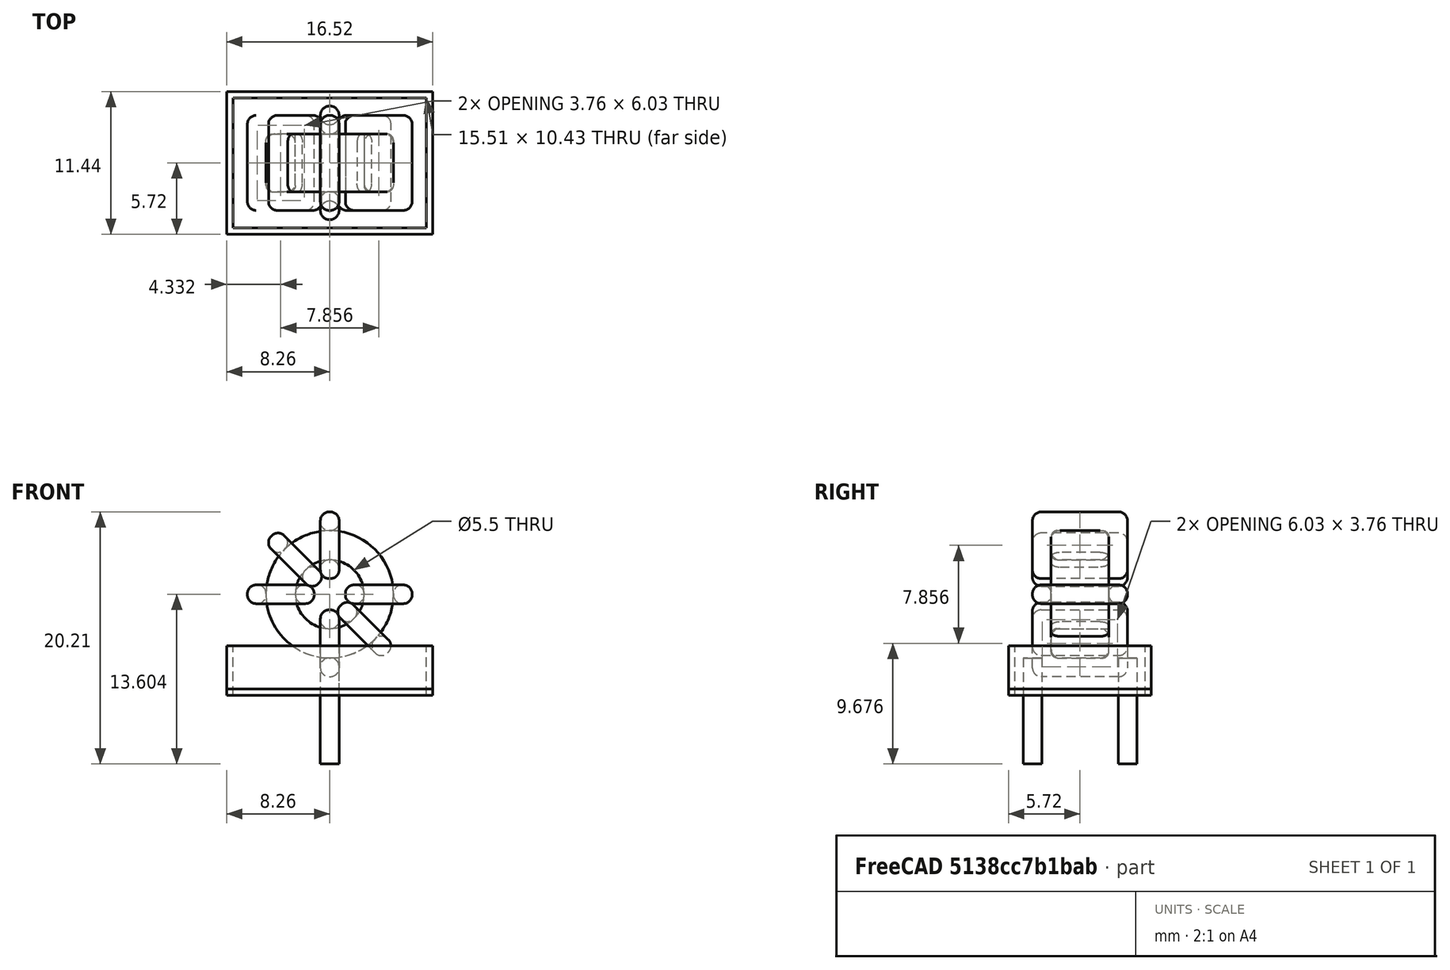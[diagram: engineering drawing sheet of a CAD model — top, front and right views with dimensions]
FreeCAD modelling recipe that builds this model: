
FCSTD DOCUMENT  (FreeCAD 0.16R6703 (Git))
Label: L_Toroid_Vertical_L16.5mm_W11.4mm_P7.62mm_Pulse_KM-2
License: All rights reserved
LicenseURL: http://en.wikipedia.org/wiki/All_rights_reserved
objects: Sketcher::SketchObject×8, PartDesign::Pad×8, PartDesign::Fillet×5, Spreadsheet::Sheet×1
note: 29 computed .brp shape members not serialized (recipe doc carries the construction recipe); baked Part::Feature solids carry a one-line shape summary decoded from their .brp

FEATURE [Spreadsheet::Sheet] Spreadsheet  label="dimensions"
  cells = A1=Wx; B1(Wx)=13.208; C1(WW)=5.503333333333334; D1(iWx)=16.51; A2=Wy; B2(Wy)=7.62; D2(iWy)=11.43; A3=RM; B3(RMx)=7.62; C3(RMy)=0; A4=d_wire; B4(d_wire)=1.5; A5=H; B5(H)=16.51; A6=offsetx; B6(offsetx)=8.255000000000001
FEATURE [Sketcher::SketchObject] Sketch
  Placement = pos=(0,-3.81,0) rot=(1,0,0;1.5708rad)
  expr: Placement.Base.y = -Spreadsheet.RMx / 2
  expr: Constraints[0] = Spreadsheet.Wx / 2 - Spreadsheet.d_wire
  expr: Constraints[4] = Spreadsheet.WW / 2
  expr: Constraints[2] = Spreadsheet.Wx / 2 + Spreadsheet.d_wire + 0.5
  sketch-geometry (2):
    g0: Circle CenterX=0 CenterY=8.604 CenterZ=0 NormalX=0 NormalY=0 NormalZ=1 Radius=5.104
    g1: Circle CenterX=0 CenterY=8.604 CenterZ=0 NormalX=0 NormalY=0 NormalZ=1 Radius=2.75167
  constraints (5):
    c: Radius(g0) = 5.104
    c: DistanceX(g-1,g0) = 0
    c: DistanceY(g-1,g0) = 8.604
    c: Coincident(g1,g0)
    c: Radius(g1) = 2.75167
FEATURE [PartDesign::Pad] Pad
  Length = 4.62
  Length2 = 100
  Midplane = true
  Placement = pos=(0,-3.81,0) rot=(1,0,0;1.5708rad)
  Sketch = -> Sketch
  Type = 0
  expr: Length = Spreadsheet.Wy - 2 * Spreadsheet.d_wire
FEATURE [Sketcher::SketchObject] Sketch001
  Placement = pos=(0,0,2) rot=(0,0,1;0rad)
  expr: Placement.Base.z = 0.5 + Spreadsheet.d_wire
  expr: Constraints[4] = Spreadsheet.RMy
  expr: Constraints[2] = -Spreadsheet.RMx
  expr: Constraints[1] = Spreadsheet.d_wire / 2
  sketch-geometry (2):
    g0: Circle CenterX=0 CenterY=0 CenterZ=0 NormalX=0 NormalY=0 NormalZ=1 Radius=0.75
    g1: Circle CenterX=0 CenterY=-7.62 CenterZ=0 NormalX=0 NormalY=0 NormalZ=1 Radius=0.75
  constraints (5):
    c: Equal(g0,g1)
    c: Radius(g0) = 0.75
    c: DistanceY(g-1,g1) = -7.62
    c: Coincident(g0,g-1)
    c: DistanceX(g-1,g1) = 0
FEATURE [PartDesign::Pad] Pad001
  Length = 1.5
  Length2 = 7
  Placement = pos=(0,0,2) rot=(0,0,1;0rad)
  Reversed = true
  Sketch = -> Sketch001
  Type = 4
  expr: Length2 = 5.5 + Spreadsheet.d_wire
  expr: Length = Spreadsheet.d_wire
FEATURE [PartDesign::Fillet] Fillet
  Base = -> Pad [Edge6,Edge3,Edge2]
  Placement = pos=(0,-3.81,0) rot=(1,0,0;1.5708rad)
  Radius = 0.5
FEATURE [Sketcher::SketchObject] Sketch003
  Placement = pos=(0,0,8.604) rot=(1,0,0;3.14159rad)
  expr: Constraints[18] = Spreadsheet.d_wire
  expr: Constraints[16] = Spreadsheet.d_wire
  expr: Constraints[19] = Spreadsheet.d_wire
  expr: Constraints[17] = Spreadsheet.d_wire
  expr: Placement.Base.y = -1 * (Spreadsheet.RMx - Spreadsheet.Wy) / 2
  expr: Constraints[21] = (Spreadsheet.Wx - Spreadsheet.WW) / 2 - Spreadsheet.d_wire
  expr: Constraints[22] = Spreadsheet.Wx / 2 - Spreadsheet.d_wire
  expr: Constraints[43] = Spreadsheet.d_wire
  expr: Constraints[48] = Spreadsheet.Wx - Spreadsheet.d_wire * 2
  expr: Constraints[49] = Spreadsheet.Wy
  expr: Placement.Base.z = Spreadsheet.Wx / 2 + Spreadsheet.d_wire + 0.5
  sketch-geometry (16):
    g0: LineSegment StartX=-1.25167 StartY=0 StartZ=0 EndX=-6.604 EndY=0 EndZ=0
    g1: LineSegment StartX=-6.604 StartY=0 StartZ=0 EndX=-6.604 EndY=7.62 EndZ=0
    g2: LineSegment StartX=-6.604 StartY=7.62 StartZ=0 EndX=-1.25167 EndY=7.62 EndZ=0
    g3: LineSegment StartX=-1.25167 StartY=7.62 StartZ=0 EndX=-1.25167 EndY=0 EndZ=0
    g4: LineSegment StartX=-5.104 StartY=6.12 StartZ=0 EndX=-2.75167 EndY=6.12 EndZ=0
    g5: LineSegment StartX=-2.75167 StartY=6.12 StartZ=0 EndX=-2.75167 EndY=1.5 EndZ=0
    g6: LineSegment StartX=-2.75167 StartY=1.5 StartZ=0 EndX=-5.104 EndY=1.5 EndZ=0
    g7: LineSegment StartX=-5.104 StartY=1.5 StartZ=0 EndX=-5.104 EndY=6.12 EndZ=0
    g8: LineSegment StartX=1.25167 StartY=7.62 StartZ=0 EndX=6.604 EndY=7.62 EndZ=0
    g9: LineSegment StartX=6.604 StartY=7.62 StartZ=0 EndX=6.604 EndY=0 EndZ=0
    g10: LineSegment StartX=6.604 StartY=0 StartZ=0 EndX=1.25167 EndY=0 EndZ=0
    g11: LineSegment StartX=1.25167 StartY=0 StartZ=0 EndX=1.25167 EndY=7.62 EndZ=0
    g12: LineSegment StartX=2.75167 StartY=6.12 StartZ=0 EndX=5.104 EndY=6.12 EndZ=0
    g13: LineSegment StartX=5.104 StartY=6.12 StartZ=0 EndX=5.104 EndY=1.5 EndZ=0
    g14: LineSegment StartX=5.104 StartY=1.5 StartZ=0 EndX=2.75167 EndY=1.5 EndZ=0
    g15: LineSegment StartX=2.75167 StartY=1.5 StartZ=0 EndX=2.75167 EndY=6.12 EndZ=0
  constraints (50):
    c: Horizontal(g0)
    c: Coincident(g1,g0)
    c: Vertical(g1)
    c: Coincident(g2,g1)
    c: Horizontal(g2)
    c: Coincident(g3,g2)
    c: Coincident(g3,g0)
    c: Vertical(g3)
    c: Coincident(g4,g5)
    c: Coincident(g5,g6)
    c: Coincident(g6,g7)
    c: Coincident(g7,g4)
    c: Horizontal(g4)
    c: Horizontal(g6)
    c: Vertical(g5)
    c: Vertical(g7)
    c: DistanceX(g1,g4) = 1.5
    c: DistanceY(g4,g1) = 1.5
    c: DistanceX(g5,g0) = 1.5
    c: DistanceY(g0,g5) = 1.5
    c: DistanceY(g-1,g0) = 0
    c: DistanceX(g6,g6) = 2.35233
    c: DistanceX(g6,g-1) = 5.104
    c: Coincident(g8,g9)
    c: Coincident(g9,g10)
    c: Coincident(g10,g11)
    c: Coincident(g11,g8)
    c: Horizontal(g8)
    c: Horizontal(g10)
    c: Vertical(g9)
    c: Vertical(g11)
    c: Coincident(g12,g13)
    c: Coincident(g13,g14)
    c: Coincident(g14,g15)
    c: Coincident(g15,g12)
    c: Horizontal(g12)
    c: Horizontal(g14)
    c: Vertical(g13)
    c: Vertical(g15)
    c: DistanceY(g8,g2) = 0
    c: DistanceY(g10,g0) = 0
    c: DistanceY(g14,g5) = 0
    c: DistanceY(g12,g4) = 0
    c: DistanceX(g8,g12) = 1.5
    c: Equal(g8,g2)
    c: Equal(g12,g4)
    c: Equal(g9,g1)
    c: Equal(g13,g7)
    c: DistanceX(g4,g12) = 10.208
    c: DistanceY(g0,g1) = 7.62
FEATURE [PartDesign::Pad] Pad002
  Length = 1.5
  Length2 = 100
  Midplane = true
  Placement = pos=(0,0,8.604) rot=(1,0,0;3.14159rad)
  Sketch = -> Sketch003
  Type = 0
  expr: Length = Spreadsheet.d_wire
FEATURE [PartDesign::Fillet] Fillet001
  Base = -> Pad002 [Edge38,Edge41,Edge42,Edge43,Edge29,Edge32,Edge33,Edge34,Edge25,Edge35,Edge36,Edge13,Edge14,Edge15,Edge16,Edge17,Edge18,Edge19,Edge1,Edge2,Edge3,Edge4,Edge5,Edge6,Edge7,Edge37,Edge39,Edge40,Edge20,Edge23,Edge24,Edge21,Edge22,Edge8,Edge9,Edge10,Edge11,Edge12,Edge26,Edge27,+8 more]
  Placement = pos=(0,0,8.604) rot=(1,0,0;3.14159rad)
  Radius = 0.705
  expr: Radius = Spreadsheet.d_wire * 0.47
FEATURE [Sketcher::SketchObject] Sketch004
  Placement = pos=(0,0,8.604) rot=(0.92388,0,0.382683;3.14159rad)
  expr: Constraints[18] = Spreadsheet.d_wire
  expr: Constraints[16] = Spreadsheet.d_wire
  expr: Constraints[19] = Spreadsheet.d_wire
  expr: Constraints[17] = Spreadsheet.d_wire
  expr: Placement.Base.y = -1 * (Spreadsheet.RMx - Spreadsheet.Wy) / 2
  expr: Constraints[21] = (Spreadsheet.Wx - Spreadsheet.WW) / 2 - Spreadsheet.d_wire
  expr: Constraints[22] = Spreadsheet.Wx / 2 - Spreadsheet.d_wire
  expr: Constraints[43] = Spreadsheet.d_wire
  expr: Constraints[48] = Spreadsheet.Wx - 2 * Spreadsheet.d_wire
  expr: Constraints[49] = Spreadsheet.Wy
  expr: Placement.Base.z = Spreadsheet.Wx / 2 + Spreadsheet.d_wire + 0.5
  sketch-geometry (16):
    g0: LineSegment StartX=-1.25167 StartY=0 StartZ=0 EndX=-6.604 EndY=0 EndZ=0
    g1: LineSegment StartX=-6.604 StartY=0 StartZ=0 EndX=-6.604 EndY=7.62 EndZ=0
    g2: LineSegment StartX=-6.604 StartY=7.62 StartZ=0 EndX=-1.25167 EndY=7.62 EndZ=0
    g3: LineSegment StartX=-1.25167 StartY=7.62 StartZ=0 EndX=-1.25167 EndY=0 EndZ=0
    g4: LineSegment StartX=-5.104 StartY=6.12 StartZ=0 EndX=-2.75167 EndY=6.12 EndZ=0
    g5: LineSegment StartX=-2.75167 StartY=6.12 StartZ=0 EndX=-2.75167 EndY=1.5 EndZ=0
    g6: LineSegment StartX=-2.75167 StartY=1.5 StartZ=0 EndX=-5.104 EndY=1.5 EndZ=0
    g7: LineSegment StartX=-5.104 StartY=1.5 StartZ=0 EndX=-5.104 EndY=6.12 EndZ=0
    g8: LineSegment StartX=1.25167 StartY=7.62 StartZ=0 EndX=6.604 EndY=7.62 EndZ=0
    g9: LineSegment StartX=6.604 StartY=7.62 StartZ=0 EndX=6.604 EndY=0 EndZ=0
    g10: LineSegment StartX=6.604 StartY=0 StartZ=0 EndX=1.25167 EndY=0 EndZ=0
    g11: LineSegment StartX=1.25167 StartY=0 StartZ=0 EndX=1.25167 EndY=7.62 EndZ=0
    g12: LineSegment StartX=2.75167 StartY=6.12 StartZ=0 EndX=5.104 EndY=6.12 EndZ=0
    g13: LineSegment StartX=5.104 StartY=6.12 StartZ=0 EndX=5.104 EndY=1.5 EndZ=0
    g14: LineSegment StartX=5.104 StartY=1.5 StartZ=0 EndX=2.75167 EndY=1.5 EndZ=0
    g15: LineSegment StartX=2.75167 StartY=1.5 StartZ=0 EndX=2.75167 EndY=6.12 EndZ=0
  constraints (50):
    c: Horizontal(g0)
    c: Coincident(g1,g0)
    c: Vertical(g1)
    c: Coincident(g2,g1)
    c: Horizontal(g2)
    c: Coincident(g3,g2)
    c: Coincident(g3,g0)
    c: Vertical(g3)
    c: Coincident(g4,g5)
    c: Coincident(g5,g6)
    c: Coincident(g6,g7)
    c: Coincident(g7,g4)
    c: Horizontal(g4)
    c: Horizontal(g6)
    c: Vertical(g5)
    c: Vertical(g7)
    c: DistanceX(g1,g4) = 1.5
    c: DistanceY(g4,g1) = 1.5
    c: DistanceX(g5,g0) = 1.5
    c: DistanceY(g0,g5) = 1.5
    c: DistanceY(g-1,g0) = 0
    c: DistanceX(g6,g6) = 2.35233
    c: DistanceX(g6,g-1) = 5.104
    c: Coincident(g8,g9)
    c: Coincident(g9,g10)
    c: Coincident(g10,g11)
    c: Coincident(g11,g8)
    c: Horizontal(g8)
    c: Horizontal(g10)
    c: Vertical(g9)
    c: Vertical(g11)
    c: Coincident(g12,g13)
    c: Coincident(g13,g14)
    c: Coincident(g14,g15)
    c: Coincident(g15,g12)
    c: Horizontal(g12)
    c: Horizontal(g14)
    c: Vertical(g13)
    c: Vertical(g15)
    c: DistanceY(g8,g2) = 0
    c: DistanceY(g10,g0) = 0
    c: DistanceY(g14,g5) = 0
    c: DistanceY(g12,g4) = 0
    c: DistanceX(g8,g12) = 1.5
    c: Equal(g8,g2)
    c: Equal(g12,g4)
    c: Equal(g9,g1)
    c: Equal(g13,g7)
    c: DistanceX(g4,g12) = 10.208
    c: DistanceY(g0,g1) = 7.62
FEATURE [PartDesign::Pad] Pad003
  Length = 1.5
  Length2 = 100
  Midplane = true
  Placement = pos=(0,0,8.604) rot=(0.92388,0,0.382683;3.14159rad)
  Sketch = -> Sketch004
  Type = 0
  expr: Length = Spreadsheet.d_wire
FEATURE [PartDesign::Fillet] Fillet002
  Base = -> Pad003 [Edge38,Edge41,Edge42,Edge43,Edge29,Edge32,Edge33,Edge34,Edge25,Edge35,Edge36,Edge13,Edge14,Edge15,Edge16,Edge17,Edge18,Edge19,Edge1,Edge2,Edge3,Edge4,Edge5,Edge6,Edge7,Edge37,Edge39,Edge40,Edge20,Edge23,Edge24,Edge21,Edge22,Edge8,Edge9,Edge10,Edge11,Edge12,Edge26,Edge27,+8 more]
  Placement = pos=(0,0,8.604) rot=(0.92388,0,0.382683;3.14159rad)
  Radius = 0.705
  expr: Radius = Spreadsheet.d_wire * 0.47
FEATURE [Sketcher::SketchObject] Sketch005
  Placement = pos=(0,0,8.604) rot=(0.92388,0,-0.382683;3.14159rad)
  expr: Constraints[18] = Spreadsheet.d_wire
  expr: Constraints[16] = Spreadsheet.d_wire
  expr: Constraints[19] = Spreadsheet.d_wire
  expr: Constraints[17] = Spreadsheet.d_wire
  expr: Placement.Base.y = -1 * (Spreadsheet.RMx - Spreadsheet.Wy) / 2
  expr: Constraints[21] = (Spreadsheet.Wx - Spreadsheet.WW) / 2 - Spreadsheet.d_wire
  expr: Constraints[22] = Spreadsheet.Wx / 2 - Spreadsheet.d_wire
  expr: Constraints[43] = Spreadsheet.d_wire
  expr: Constraints[48] = Spreadsheet.Wx - 2 * Spreadsheet.d_wire
  expr: Constraints[49] = Spreadsheet.Wy
  expr: Placement.Base.z = Spreadsheet.Wx / 2 + Spreadsheet.d_wire + 0.5
  sketch-geometry (16):
    g0: LineSegment StartX=-1.25167 StartY=0 StartZ=0 EndX=-6.604 EndY=0 EndZ=0
    g1: LineSegment StartX=-6.604 StartY=0 StartZ=0 EndX=-6.604 EndY=7.62 EndZ=0
    g2: LineSegment StartX=-6.604 StartY=7.62 StartZ=0 EndX=-1.25167 EndY=7.62 EndZ=0
    g3: LineSegment StartX=-1.25167 StartY=7.62 StartZ=0 EndX=-1.25167 EndY=0 EndZ=0
    g4: LineSegment StartX=-5.104 StartY=6.12 StartZ=0 EndX=-2.75167 EndY=6.12 EndZ=0
    g5: LineSegment StartX=-2.75167 StartY=6.12 StartZ=0 EndX=-2.75167 EndY=1.5 EndZ=0
    g6: LineSegment StartX=-2.75167 StartY=1.5 StartZ=0 EndX=-5.104 EndY=1.5 EndZ=0
    g7: LineSegment StartX=-5.104 StartY=1.5 StartZ=0 EndX=-5.104 EndY=6.12 EndZ=0
    g8: LineSegment StartX=1.25167 StartY=7.62 StartZ=0 EndX=6.604 EndY=7.62 EndZ=0
    g9: LineSegment StartX=6.604 StartY=7.62 StartZ=0 EndX=6.604 EndY=0 EndZ=0
    g10: LineSegment StartX=6.604 StartY=0 StartZ=0 EndX=1.25167 EndY=0 EndZ=0
    g11: LineSegment StartX=1.25167 StartY=0 StartZ=0 EndX=1.25167 EndY=7.62 EndZ=0
    g12: LineSegment StartX=2.75167 StartY=6.12 StartZ=0 EndX=5.104 EndY=6.12 EndZ=0
    g13: LineSegment StartX=5.104 StartY=6.12 StartZ=0 EndX=5.104 EndY=1.5 EndZ=0
    g14: LineSegment StartX=5.104 StartY=1.5 StartZ=0 EndX=2.75167 EndY=1.5 EndZ=0
    g15: LineSegment StartX=2.75167 StartY=1.5 StartZ=0 EndX=2.75167 EndY=6.12 EndZ=0
  constraints (50):
    c: Horizontal(g0)
    c: Coincident(g1,g0)
    c: Vertical(g1)
    c: Coincident(g2,g1)
    c: Horizontal(g2)
    c: Coincident(g3,g2)
    c: Coincident(g3,g0)
    c: Vertical(g3)
    c: Coincident(g4,g5)
    c: Coincident(g5,g6)
    c: Coincident(g6,g7)
    c: Coincident(g7,g4)
    c: Horizontal(g4)
    c: Horizontal(g6)
    c: Vertical(g5)
    c: Vertical(g7)
    c: DistanceX(g1,g4) = 1.5
    c: DistanceY(g4,g1) = 1.5
    c: DistanceX(g5,g0) = 1.5
    c: DistanceY(g0,g5) = 1.5
    c: DistanceY(g-1,g0) = 0
    c: DistanceX(g6,g6) = 2.35233
    c: DistanceX(g6,g-1) = 5.104
    c: Coincident(g8,g9)
    c: Coincident(g9,g10)
    c: Coincident(g10,g11)
    c: Coincident(g11,g8)
    c: Horizontal(g8)
    c: Horizontal(g10)
    c: Vertical(g9)
    c: Vertical(g11)
    c: Coincident(g12,g13)
    c: Coincident(g13,g14)
    c: Coincident(g14,g15)
    c: Coincident(g15,g12)
    c: Horizontal(g12)
    c: Horizontal(g14)
    c: Vertical(g13)
    c: Vertical(g15)
    c: DistanceY(g8,g2) = 0
    c: DistanceY(g10,g0) = 0
    c: DistanceY(g14,g5) = 0
    c: DistanceY(g12,g4) = 0
    c: DistanceX(g8,g12) = 1.5
    c: Equal(g8,g2)
    c: Equal(g12,g4)
    c: Equal(g9,g1)
    c: Equal(g13,g7)
    c: DistanceX(g4,g12) = 10.208
    c: DistanceY(g0,g1) = 7.62
FEATURE [PartDesign::Pad] Pad004
  Length = 1.5
  Length2 = 100
  Midplane = true
  Placement = pos=(0,0,8.604) rot=(0.92388,0,-0.382683;3.14159rad)
  Sketch = -> Sketch005
  Type = 0
  expr: Length = Spreadsheet.d_wire
FEATURE [PartDesign::Fillet] Fillet003
  Base = -> Pad004 [Edge38,Edge41,Edge42,Edge43,Edge29,Edge32,Edge33,Edge34,Edge25,Edge35,Edge36,Edge13,Edge14,Edge15,Edge16,Edge17,Edge18,Edge19,Edge1,Edge2,Edge3,Edge4,Edge5,Edge6,Edge7,Edge37,Edge39,Edge40,Edge20,Edge23,Edge24,Edge21,Edge22,Edge8,Edge9,Edge10,Edge11,Edge12,Edge26,Edge27,+8 more]
  Placement = pos=(0,0,8.604) rot=(0.92388,0,-0.382683;3.14159rad)
  Radius = 0.705
  expr: Radius = Spreadsheet.d_wire * 0.47
FEATURE [Sketcher::SketchObject] Sketch006
  Placement = pos=(0,0,8.604) rot=(0.707107,0,0.707107;3.14159rad)
  expr: Constraints[18] = Spreadsheet.d_wire
  expr: Constraints[16] = Spreadsheet.d_wire
  expr: Constraints[19] = Spreadsheet.d_wire
  expr: Constraints[17] = Spreadsheet.d_wire
  expr: Placement.Base.y = -1 * (Spreadsheet.RMx - Spreadsheet.Wy) / 2
  expr: Constraints[21] = (Spreadsheet.Wx - Spreadsheet.WW) / 2 - Spreadsheet.d_wire
  expr: Constraints[22] = Spreadsheet.Wx / 2 - Spreadsheet.d_wire
  expr: Constraints[43] = Spreadsheet.d_wire
  expr: Constraints[48] = Spreadsheet.Wx - Spreadsheet.d_wire * 2
  expr: Constraints[49] = Spreadsheet.Wy
  expr: Placement.Base.z = Spreadsheet.Wx / 2 + Spreadsheet.d_wire + 0.5
  sketch-geometry (16):
    g0: LineSegment StartX=-1.25167 StartY=0 StartZ=0 EndX=-6.604 EndY=0 EndZ=0
    g1: LineSegment StartX=-6.604 StartY=0 StartZ=0 EndX=-6.604 EndY=7.62 EndZ=0
    g2: LineSegment StartX=-6.604 StartY=7.62 StartZ=0 EndX=-1.25167 EndY=7.62 EndZ=0
    g3: LineSegment StartX=-1.25167 StartY=7.62 StartZ=0 EndX=-1.25167 EndY=0 EndZ=0
    g4: LineSegment StartX=-5.104 StartY=6.12 StartZ=0 EndX=-2.75167 EndY=6.12 EndZ=0
    g5: LineSegment StartX=-2.75167 StartY=6.12 StartZ=0 EndX=-2.75167 EndY=1.5 EndZ=0
    g6: LineSegment StartX=-2.75167 StartY=1.5 StartZ=0 EndX=-5.104 EndY=1.5 EndZ=0
    g7: LineSegment StartX=-5.104 StartY=1.5 StartZ=0 EndX=-5.104 EndY=6.12 EndZ=0
    g8: LineSegment StartX=1.25167 StartY=7.62 StartZ=0 EndX=6.604 EndY=7.62 EndZ=0
    g9: LineSegment StartX=6.604 StartY=7.62 StartZ=0 EndX=6.604 EndY=0 EndZ=0
    g10: LineSegment StartX=6.604 StartY=0 StartZ=0 EndX=1.25167 EndY=0 EndZ=0
    g11: LineSegment StartX=1.25167 StartY=0 StartZ=0 EndX=1.25167 EndY=7.62 EndZ=0
    g12: LineSegment StartX=2.75167 StartY=6.12 StartZ=0 EndX=5.104 EndY=6.12 EndZ=0
    g13: LineSegment StartX=5.104 StartY=6.12 StartZ=0 EndX=5.104 EndY=1.5 EndZ=0
    g14: LineSegment StartX=5.104 StartY=1.5 StartZ=0 EndX=2.75167 EndY=1.5 EndZ=0
    g15: LineSegment StartX=2.75167 StartY=1.5 StartZ=0 EndX=2.75167 EndY=6.12 EndZ=0
  constraints (50):
    c: Horizontal(g0)
    c: Coincident(g1,g0)
    c: Vertical(g1)
    c: Coincident(g2,g1)
    c: Horizontal(g2)
    c: Coincident(g3,g2)
    c: Coincident(g3,g0)
    c: Vertical(g3)
    c: Coincident(g4,g5)
    c: Coincident(g5,g6)
    c: Coincident(g6,g7)
    c: Coincident(g7,g4)
    c: Horizontal(g4)
    c: Horizontal(g6)
    c: Vertical(g5)
    c: Vertical(g7)
    c: DistanceX(g1,g4) = 1.5
    c: DistanceY(g4,g1) = 1.5
    c: DistanceX(g5,g0) = 1.5
    c: DistanceY(g0,g5) = 1.5
    c: DistanceY(g-1,g0) = 0
    c: DistanceX(g6,g6) = 2.35233
    c: DistanceX(g6,g-1) = 5.104
    c: Coincident(g8,g9)
    c: Coincident(g9,g10)
    c: Coincident(g10,g11)
    c: Coincident(g11,g8)
    c: Horizontal(g8)
    c: Horizontal(g10)
    c: Vertical(g9)
    c: Vertical(g11)
    c: Coincident(g12,g13)
    c: Coincident(g13,g14)
    c: Coincident(g14,g15)
    c: Coincident(g15,g12)
    c: Horizontal(g12)
    c: Horizontal(g14)
    c: Vertical(g13)
    c: Vertical(g15)
    c: DistanceY(g8,g2) = 0
    c: DistanceY(g10,g0) = 0
    c: DistanceY(g14,g5) = 0
    c: DistanceY(g12,g4) = 0
    c: DistanceX(g8,g12) = 1.5
    c: Equal(g8,g2)
    c: Equal(g12,g4)
    c: Equal(g9,g1)
    c: Equal(g13,g7)
    c: DistanceX(g4,g12) = 10.208
    c: DistanceY(g0,g1) = 7.62
FEATURE [PartDesign::Pad] Pad005
  Length = 1.5
  Length2 = 100
  Midplane = true
  Placement = pos=(0,0,8.604) rot=(0.707107,0,0.707107;3.14159rad)
  Sketch = -> Sketch006
  Type = 0
  expr: Length = Spreadsheet.d_wire
FEATURE [PartDesign::Fillet] Fillet004
  Base = -> Pad005 [Edge38,Edge41,Edge42,Edge43,Edge29,Edge32,Edge33,Edge34,Edge25,Edge35,Edge36,Edge13,Edge14,Edge15,Edge16,Edge17,Edge18,Edge19,Edge1,Edge2,Edge3,Edge4,Edge5,Edge6,Edge7,Edge37,Edge39,Edge40,Edge20,Edge23,Edge24,Edge21,Edge22,Edge8,Edge9,Edge10,Edge11,Edge12,Edge26,Edge27,+8 more]
  Placement = pos=(0,0,8.604) rot=(0.707107,0,0.707107;3.14159rad)
  Radius = 0.705
  expr: Radius = Spreadsheet.d_wire * 0.47
FEATURE [Sketcher::SketchObject] Sketch007
  Placement = pos=(0,0,0.5) rot=(0,0,1;0rad)
  expr: Placement.Base.z = 0.5
  expr: Constraints[11] = Spreadsheet.iWx / 2
  expr: Constraints[10] = (Spreadsheet.iWy - Spreadsheet.RMx) / 2
  expr: Constraints[9] = Spreadsheet.iWy
  expr: Constraints[8] = Spreadsheet.iWx
  sketch-geometry (4):
    g0: LineSegment StartX=-8.255 StartY=1.905 StartZ=0 EndX=8.255 EndY=1.905 EndZ=0
    g1: LineSegment StartX=8.255 StartY=1.905 StartZ=0 EndX=8.255 EndY=-9.525 EndZ=0
    g2: LineSegment StartX=8.255 StartY=-9.525 StartZ=0 EndX=-8.255 EndY=-9.525 EndZ=0
    g3: LineSegment StartX=-8.255 StartY=-9.525 StartZ=0 EndX=-8.255 EndY=1.905 EndZ=0
  constraints (12):
    c: Coincident(g0,g1)
    c: Coincident(g1,g2)
    c: Coincident(g2,g3)
    c: Coincident(g3,g0)
    c: Horizontal(g0)
    c: Horizontal(g2)
    c: Vertical(g1)
    c: Vertical(g3)
    c: DistanceX(g0,g0) = 16.51
    c: DistanceY(g3,g3) = 11.43
    c: DistanceY(g-1,g0) = 1.905
    c: DistanceX(g0,g-1) = 8.255
FEATURE [PartDesign::Pad] Pad006
  Length = 0.5
  Length2 = 100
  Placement = pos=(0,0,0.5) rot=(0,0,1;0rad)
  Sketch = -> Sketch007
  Type = 0
FEATURE [Sketcher::SketchObject] Sketch008
  Placement = pos=(0,0,0.5) rot=(0,0,1;0rad)
  expr: Constraints[8] = Spreadsheet.iWx
  expr: Constraints[9] = Spreadsheet.iWy
  expr: Constraints[10] = (Spreadsheet.iWy - Spreadsheet.RMx) / 2
  expr: Placement.Base.z = 0.5
  expr: Constraints[21] = 0.5
  expr: Constraints[11] = Spreadsheet.iWx / 2
  sketch-geometry (8):
    g0: LineSegment StartX=-8.255 StartY=1.905 StartZ=0 EndX=8.255 EndY=1.905 EndZ=0
    g1: LineSegment StartX=8.255 StartY=1.905 StartZ=0 EndX=8.255 EndY=-9.525 EndZ=0
    g2: LineSegment StartX=8.255 StartY=-9.525 StartZ=0 EndX=-8.255 EndY=-9.525 EndZ=0
    g3: LineSegment StartX=-8.255 StartY=-9.525 StartZ=0 EndX=-8.255 EndY=1.905 EndZ=0
    g4: LineSegment StartX=-7.755 StartY=1.405 StartZ=0 EndX=7.755 EndY=1.405 EndZ=0
    g5: LineSegment StartX=7.755 StartY=1.405 StartZ=0 EndX=7.755 EndY=-9.025 EndZ=0
    g6: LineSegment StartX=7.755 StartY=-9.025 StartZ=0 EndX=-7.755 EndY=-9.025 EndZ=0
    g7: LineSegment StartX=-7.755 StartY=-9.025 StartZ=0 EndX=-7.755 EndY=1.405 EndZ=0
  constraints (24):
    c: Coincident(g0,g1)
    c: Coincident(g1,g2)
    c: Coincident(g2,g3)
    c: Coincident(g3,g0)
    c: Horizontal(g0)
    c: Horizontal(g2)
    c: Vertical(g1)
    c: Vertical(g3)
    c: DistanceX(g0,g0) = 16.51
    c: DistanceY(g3,g3) = 11.43
    c: DistanceY(g-1,g0) = 1.905
    c: DistanceX(g0,g-1) = 8.255
    c: Coincident(g4,g5)
    c: Coincident(g5,g6)
    c: Coincident(g6,g7)
    c: Coincident(g7,g4)
    c: Horizontal(g4)
    c: Horizontal(g6)
    c: Vertical(g5)
    c: Vertical(g7)
    c: DistanceX(g5,g1) = 0.5
    c: DistanceY(g1,g5) = 0.5
    c: DistanceX(g0,g4) = 0.5
    c: DistanceY(g4,g0) = 0.5
FEATURE [PartDesign::Pad] Pad007
  Length = 3.9624
  Length2 = 100
  Placement = pos=(0,0,0.5) rot=(0,0,1;0rad)
  Sketch = -> Sketch008
  Type = 0
  expr: Length = Spreadsheet.Wx * 0.3
